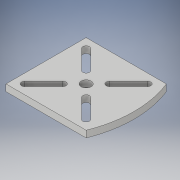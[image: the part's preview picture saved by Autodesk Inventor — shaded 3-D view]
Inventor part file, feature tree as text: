
AUTODESK INVENTOR PART (.ipt)
format: ipt  version: 2018 (Build 220112000, 112)  size: 146,944 bytes
history: native  units: in
note: dims shown in document units (in); Inventor stores cm internally (conversion verified against a paired STEP export)
features: extrude x3, sketch x3
ambient origin geometry x8: Origin, YZ Plane, XZ Plane, XY Plane, X Axis, Y Axis, Z Axis, Center Point
bodies: Solid1 (feature_tree)
feature tree (6):
  extrude  "Extrusion1"  Depth=12.0in
  extrude  "Extrusion2"  Depth=1.0in
  extrude  "Extrusion3"  Depth=1.0in TaperAngle=0.0deg
  sketch  "Sketch1"  dims[d0=12.0in d1=12.0in]
  sketch  "Sketch2"  dims[d2=1.0in d3=0.0in d4=6.0in]
  sketch  "Sketch3"  dims[d5=1.5in d6=2.0in d7=0.0in d8=2.0in d9=2.0in d10=2.0in d11=2.0in d12=4.0in d13=1.0in d14=4.0in d15=1.0in d16=4.0in d17=1.0in d18=4.0in d19=1.0in d20=2.0in d21=0.0in]
